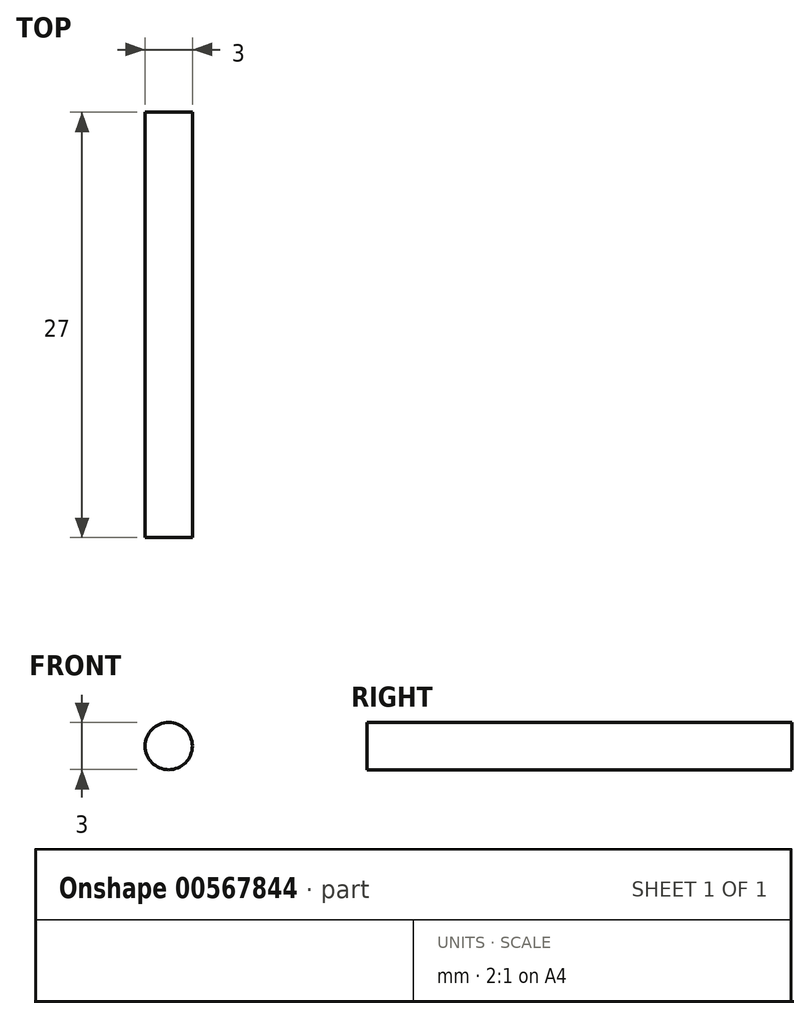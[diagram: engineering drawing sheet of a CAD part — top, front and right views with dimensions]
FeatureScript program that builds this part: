
annotation { "Feature Type Name" : "Feature", "Feature Type Description" : "" }
export const myFeature = defineFeature(function(context is Context, id is Id, definition is map)
    precondition{}
    {
        {
            var Q0;
            Q0=qCreatedBy(makeId("Front.planeOp"),FACE);
            var sketch = newSketch(context, id + "F0", { "sketchPlane" : qUnion([Q0])});
            skCircle(sketch, "E0", {"center": v(-58.5, 61.44) * mm, "radius": 1.5 * mm});
            skSolve(sketch);
        }
        {
            var Q0;
            Q0 = qSketchRegion(id + "F0", true);
            extrude(context, id + "F1", {"entities" : qUnion([Q0]), "depth" : 27 * mm, "offsetDistance" : 25.4 * mm});
        }
    });
